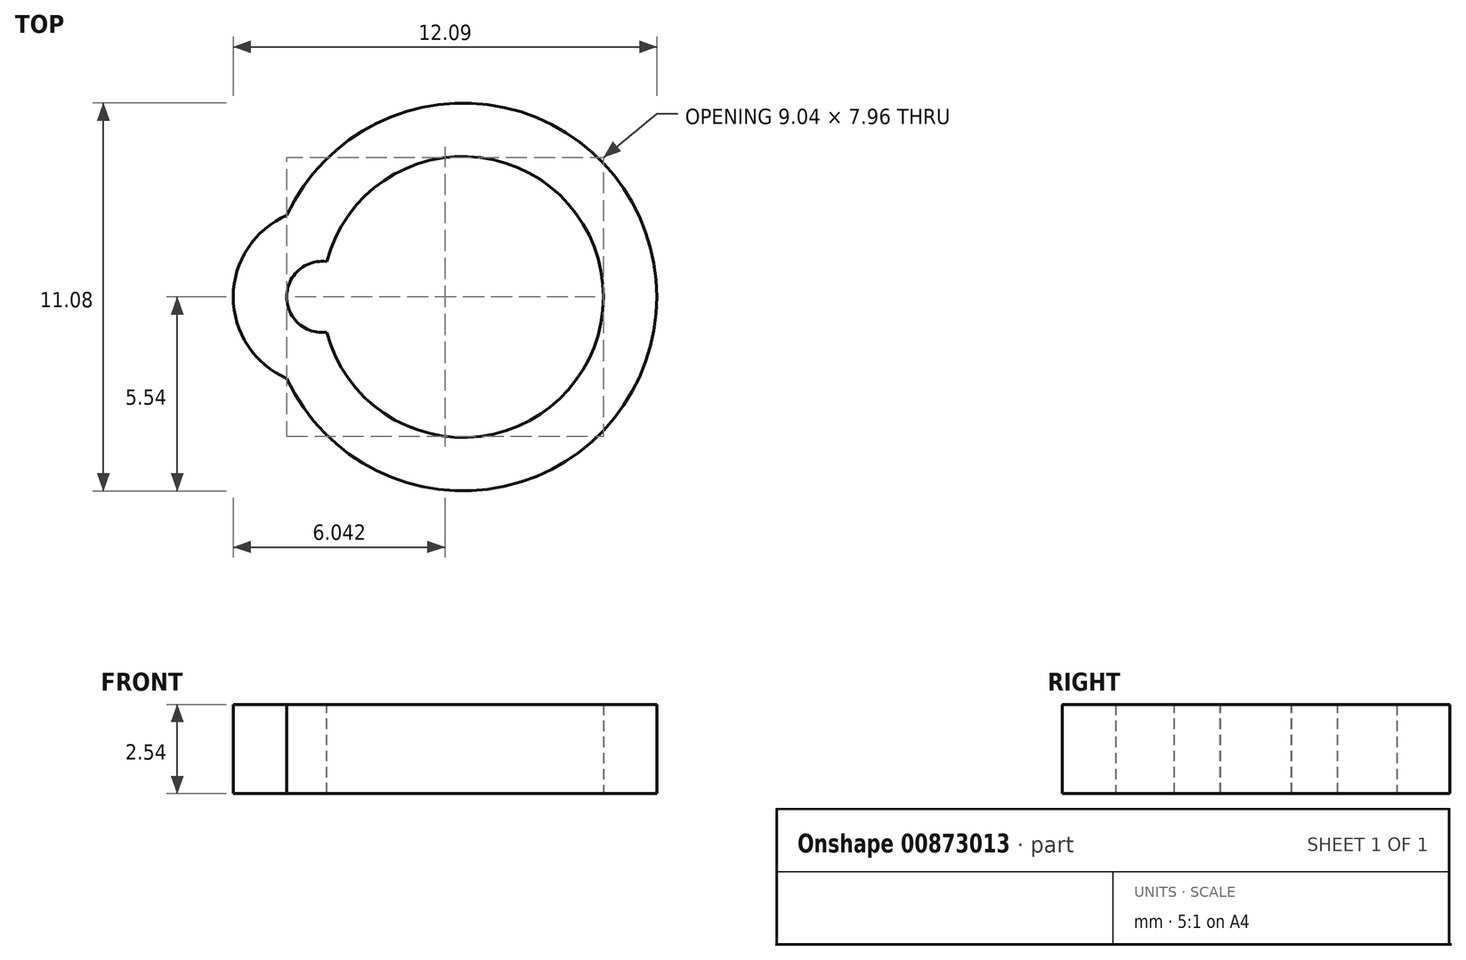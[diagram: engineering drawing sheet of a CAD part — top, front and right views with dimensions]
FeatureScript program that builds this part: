
annotation { "Feature Type Name" : "Feature", "Feature Type Description" : "" }
export const myFeature = defineFeature(function(context is Context, id is Id, definition is map)
    precondition{}
    {
        {
            var Q0;
            Q0=qCreatedBy(makeId("Top.planeOp"),FACE);
            var sketch = newSketch(context, id + "F0", { "sketchPlane" : qUnion([Q0])});
            skCircle(sketch, "E0", {"center": v(0, 0) * mm, "radius": 5.54 * mm});
            skCircle(sketch, "E1", {"center": v(0, 0) * mm, "radius": 4.01 * mm});
            skSolve(sketch);
        }
        {
            var Q0;
            Q0=makeQuery(id+"F0.imprint","IMPRINT",FACE,{"disambiguationData":[TD([[makeQuery(id+"F0.imprint","IMPRINT",EDGE,{"derivedFrom":sQuery(id+"F0.wireOp",EDGE,"E0")}),1.0]])]});
            extrude(context, id + "F1", {"entities" : qUnion([Q0]), "depth" : 2.54 * mm, "offsetDistance" : 25.4 * mm});
        }
        {
            var Q0;
            Q0=makeQuery(id+"F1.opExtrude","CAP_FACE",FACE,{"disambiguationData":[OSD([sQuery(id+"F0.wireOp",EDGE,"E0"),sQuery(id+"F0.wireOp",EDGE,"E1")])],"isStart":false});
            var sketch = newSketch(context, id + "F2", { "sketchPlane" : qUnion([Q0])});
            skArc(sketch, "E2", {"start": v(-3.88, 1) * mm, "mid": v(-5.03, 0) * mm, "end": v(-3.88, -1) * mm});
            skArc(sketch, "E3", {"start": v(-5.02, 2.33) * mm, "mid": v(-6.55, 0) * mm, "end": v(-5.02, -2.33) * mm});
            skArc(sketch, "E4.0", {"start": v(-3.88, 1) * mm, "mid": v(-4.01, 0) * mm, "end": v(-3.88, -1) * mm});
            skArc(sketch, "E5.0", {"start": v(-5.02, 2.33) * mm, "mid": v(-5.54, 0) * mm, "end": v(-5.02, -2.33) * mm});
            skSolve(sketch);
        }
        {
            var Q0;
            Q0=makeQuery(id+"F2.imprint","IMPRINT",FACE,{"disambiguationData":[TD([[makeQuery(id+"F2.imprint","IMPRINT",EDGE,{"derivedFrom":sQuery(id+"F2.wireOp",EDGE,"E2")}),1.0]])]});
            extrude(context, id + "F3", {"entities" : qUnion([Q0]), "operationType" : NewBodyOperationType.REMOVE, "endBound" : BoundingType.THROUGH_ALL, "oppositeDirection" : true, "depth" : 25.4 * mm, "offsetDistance" : 25.4 * mm});
        }
        {
            var Q0;
            {var subQ0=sQuery(id+"F2.wireOp",EDGE,"E2");Q0=makeQuery(id+"F2.imprint","IMPRINT",FACE,{"disambiguationData":[TD([[makeQuery(id+"F2.imprint","IMPRINT",EDGE,{"derivedFrom":subQ0}),-1.0]])]});}
            var sketch = newSketch(context, id + "F4", { "sketchPlane" : qUnion([Q0])});
            skArc(sketch, "E6.0", {"start": v(-5.02, 2.33) * mm, "mid": v(-5.54, 0) * mm, "end": v(-5.02, -2.33) * mm});
            skArc(sketch, "E7.0", {"start": v(-5.02, 2.33) * mm, "mid": v(-6.55, 0) * mm, "end": v(-5.02, -2.33) * mm});
            skSolve(sketch);
        }
        {
            var Q0;
            Q0 = qSketchRegion(id + "F4", true);
            var Q1;
            Q1=makeQuery(id+"F1.opExtrude","CAP_FACE",FACE,{"disambiguationData":[OSD([sQuery(id+"F0.wireOp",EDGE,"E0"),sQuery(id+"F0.wireOp",EDGE,"E1")])],"isStart":true});
            extrude(context, id + "F5", {"entities" : qUnion([Q0]), "operationType" : NewBodyOperationType.ADD, "endBound" : BoundingType.UP_TO_SURFACE, "oppositeDirection" : true, "depth" : 25.4 * mm, "endBoundEntityFace" : qUnion([Q1]), "offsetDistance" : 25.4 * mm});
        }
    });
